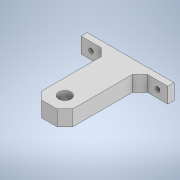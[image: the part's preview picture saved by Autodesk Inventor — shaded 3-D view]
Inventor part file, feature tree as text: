
AUTODESK INVENTOR PART (.ipt)
format: ipt  version: 2022 (Build 260153000, 153)  size: 128,000 bytes
history: native  units: mm
features: sketch x3, extrude x2, hole x2, other x1, chamfer x1
ambient origin geometry x8: Origin, YZ Plane, XZ Plane, XY Plane, X Axis, Y Axis, Z Axis, Center Point
bodies: Body1 (feature_tree)
feature tree (9):
  other  "Sólido1"
  sketch  "Esboço1"  dims[d0=56.0mm d1=10.0mm]
  extrude  "Extrusão1"  Depth=10.0mm
  extrude  "Extrusão2"  Depth=4.0mm TaperAngle=0.0deg
  chamfer  "Chanfro1"  Distance=52.426mm
  hole  "Furo1"  [1 undecoded]
  hole  "Furo2"  [1 undecoded]
  sketch  "Esboço2"  dims[d2=20.0mm d3=4.0mm d4=0.0mm d5=52.426mm d6=0.0mm]
  sketch  "Esboço3"  dims[d7=5.0mm d8=2.0mm d9=45.0deg d10=8.0mm d11=6.0mm d12=4.0mm d13=2.0mm d14=90.0deg d15=8.0mm d16=20.594885mm d17=3.0mm d18=6.0mm d19=4.0mm d20=2.0mm d21=90.0deg d22=8.0mm d23=20.594885mm d24=10.0mm]
note: 2 required parameter values undecoded (feature->parameter linkage not recoverable at this tier; creation-order binding heuristic only, values carry confidence <= 0.55)
